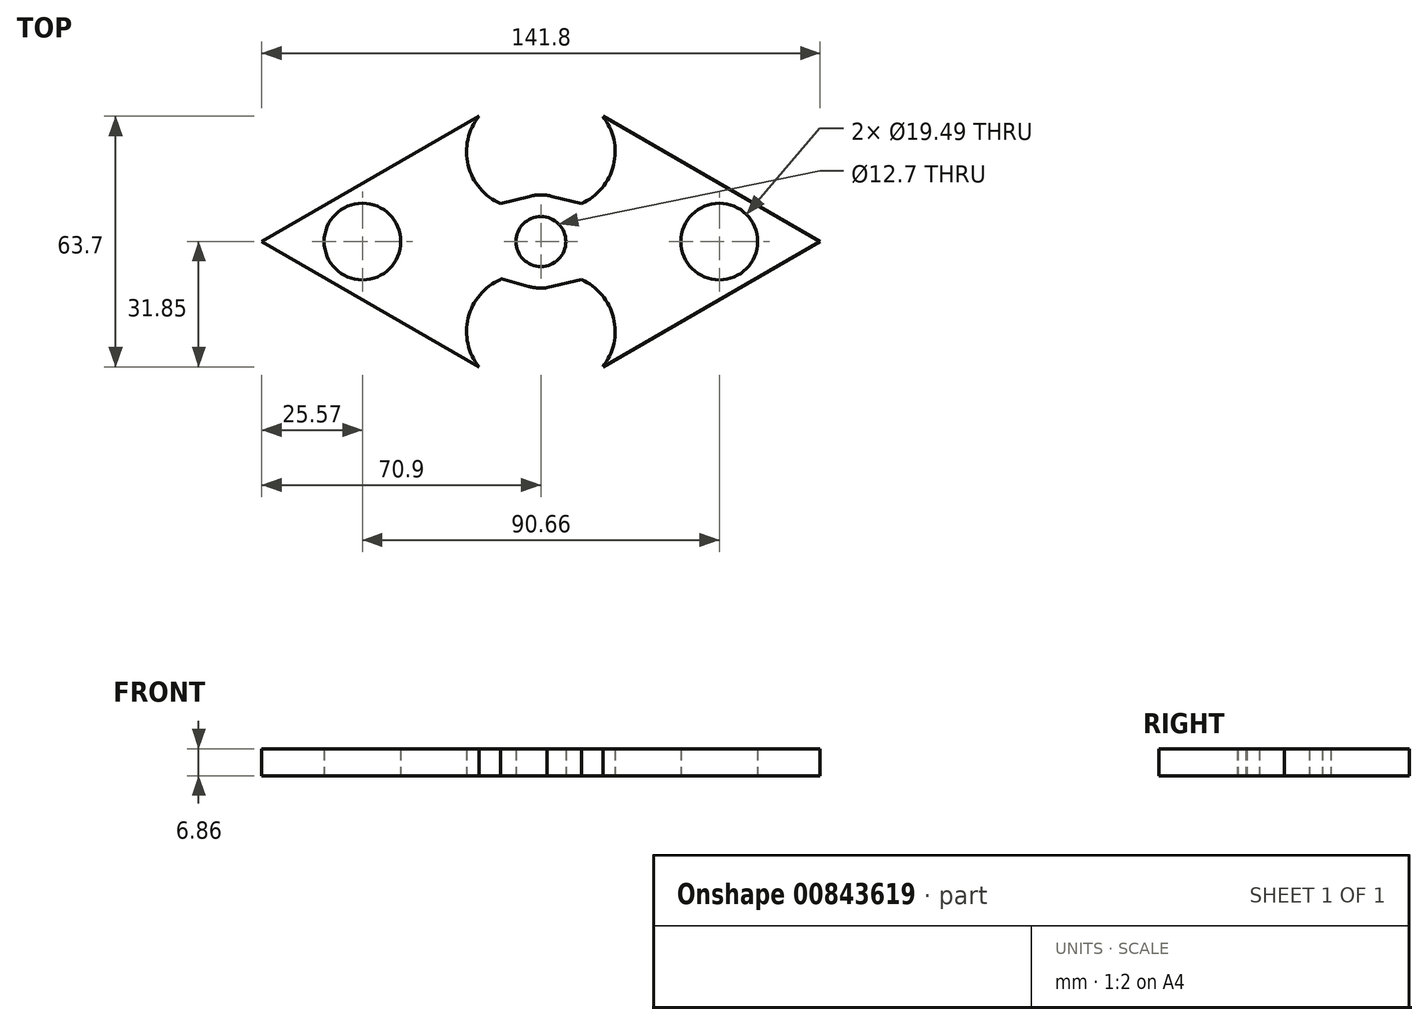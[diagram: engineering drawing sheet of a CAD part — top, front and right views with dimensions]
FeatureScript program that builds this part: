
annotation { "Feature Type Name" : "Feature", "Feature Type Description" : "" }
export const myFeature = defineFeature(function(context is Context, id is Id, definition is map)
    precondition{}
    {
        {
            var Q0;
            Q0=qCreatedBy(makeId("Top.planeOp"),FACE);
            var sketch = newSketch(context, id + "F0", { "sketchPlane" : qUnion([Q0])});
            skCircle(sketch, "E0", {"center": v(0, 0) * mm, "radius": 6.35 * mm});
            skLineSegment(sketch, "E1", {"start": v(0, 0) * mm, "end": v(52.85, 0) * mm});
            skLineSegment(sketch, "E2", {"start": v(52.85, 0) * mm, "end": v(-45.33, 0) * mm});
            skLineSegment(sketch, "E3.0", {"start": v(-10.27, -9.42) * mm, "end": v(-10.27, -9.65) * mm});
            skLineSegment(sketch, "E3.1", {"start": v(-15.72, -31.85) * mm, "end": v(-70.9, 0) * mm});
            skLineSegment(sketch, "E3.2", {"start": v(-70.9, 0) * mm, "end": v(-15.72, 31.85) * mm});
            skPoint(sketch, "E3.0.midPoint", {"position": v(-10.27, 0) * mm});
            skArc(sketch, "E4", {"start": v(-15.72, 31.85) * mm, "mid": v(-18.47, 19.41) * mm, "end": v(-10.27, 9.65) * mm});
            skArc(sketch, "E5.MirrorC", {"start": v(-15.72, -31.85) * mm, "mid": v(-18.47, -19.41) * mm, "end": v(-10.27, -9.65) * mm});
            skLineSegment(sketch, "E6.MirrorCS", {"start": v(-10.27, -9.65) * mm, "end": v(-10.27, -9.42) * mm});
            skPoint(sketch, "E7.orphan", {"position": v(-10.27, 35) * mm});
            skPoint(sketch, "E8.orphan", {"position": v(-10.27, -35) * mm});
            skLineSegment(sketch, "E9.bottom", {"start": v(-6.35, 0) * mm, "end": v(-5.6, 0) * mm});
            skPoint(sketch, "E10.orphan", {"position": v(-5.6, -9.42) * mm});
            skPoint(sketch, "E9.top.end.orphan", {"position": v(-7.93, -9.42) * mm});
            skCircle(sketch, "E11", {"center": v(-45.33, 0) * mm, "radius": 9.74 * mm});
            skLineSegment(sketch, "E12", {"start": v(-10.27, 9.65) * mm, "end": v(-2.84, 11.5) * mm});
            skLineSegment(sketch, "E13", {"start": v(-10.27, -9.42) * mm, "end": v(-3.19, -11.4) * mm});
            skPoint(sketch, "E3.cCircle.center.orphan", {"position": v(-30.48, 0) * mm});
            skArc(sketch, "E14.trimOffspring", {"start": v(-3.19, -11.4) * mm, "mid": v(0.4, -11.83) * mm, "end": v(3.94, -11.16) * mm});
            skLineSegment(sketch, "E15.1.0", {"start": v(70.9, 0) * mm, "end": v(15.72, -31.85) * mm});
            skPoint(sketch, "E15.1.1", {"position": v(5.6, 9.42) * mm});
            skPoint(sketch, "E15.1.2", {"position": v(10.27, 0) * mm});
            skLineSegment(sketch, "E15.1.3", {"start": v(6.35, 0) * mm, "end": v(5.6, 0) * mm});
            skPoint(sketch, "E15.1.4", {"position": v(10.27, 35) * mm});
            skArc(sketch, "E15.1.5", {"start": v(15.72, 31.85) * mm, "mid": v(18.47, 19.41) * mm, "end": v(10.27, 9.65) * mm});
            skLineSegment(sketch, "E15.1.6", {"start": v(15.72, 31.85) * mm, "end": v(70.9, 0) * mm});
            skPoint(sketch, "E15.1.7", {"position": v(7.93, 9.42) * mm});
            skPoint(sketch, "E15.1.8", {"position": v(10.27, -35) * mm});
            skPoint(sketch, "E15.1.9", {"position": v(30.48, 0) * mm});
            skCircle(sketch, "E15.1.10", {"center": v(45.33, 0) * mm, "radius": 9.74 * mm});
            skArc(sketch, "E15.1.11", {"start": v(15.72, -31.85) * mm, "mid": v(18.47, -19.41) * mm, "end": v(10.27, -9.65) * mm});
            skPoint(sketch, "E15.1.12", {"position": v(10.27, -35) * mm});
            skPoint(sketch, "E15.1.13", {"position": v(10.27, 35) * mm});
            skLineSegment(sketch, "E15.1.14", {"start": v(10.27, 9.65) * mm, "end": v(10.27, 9.42) * mm});
            skLineSegment(sketch, "E15.1.15", {"start": v(10.27, 9.42) * mm, "end": v(10.27, 9.65) * mm});
            skLineSegment(sketch, "E16", {"start": v(10.27, 9.65) * mm, "end": v(2.84, 11.5) * mm});
            skLineSegment(sketch, "E17", {"start": v(10.27, -9.65) * mm, "end": v(1.51, -11.74) * mm});
            skArc(sketch, "E18.trimOffspring", {"start": v(2.84, 11.5) * mm, "mid": v(0, 11.84) * mm, "end": v(-2.84, 11.5) * mm});
            skSolve(sketch);
        }
        {
            var Q0;
            Q0=makeQuery(id+"F0.imprint","IMPRINT",FACE,{"disambiguationData":[TD([[makeQuery(id+"F0.imprint","IMPRINT",EDGE,{"derivedFrom":sQuery(id+"F0.wireOp",EDGE,"E3.1")}),-1.0]])]});
            extrude(context, id + "F1", {"entities" : qUnion([Q0]), "depth" : 6.86 * mm, "offsetDistance" : 25.4 * mm});
        }
    });
